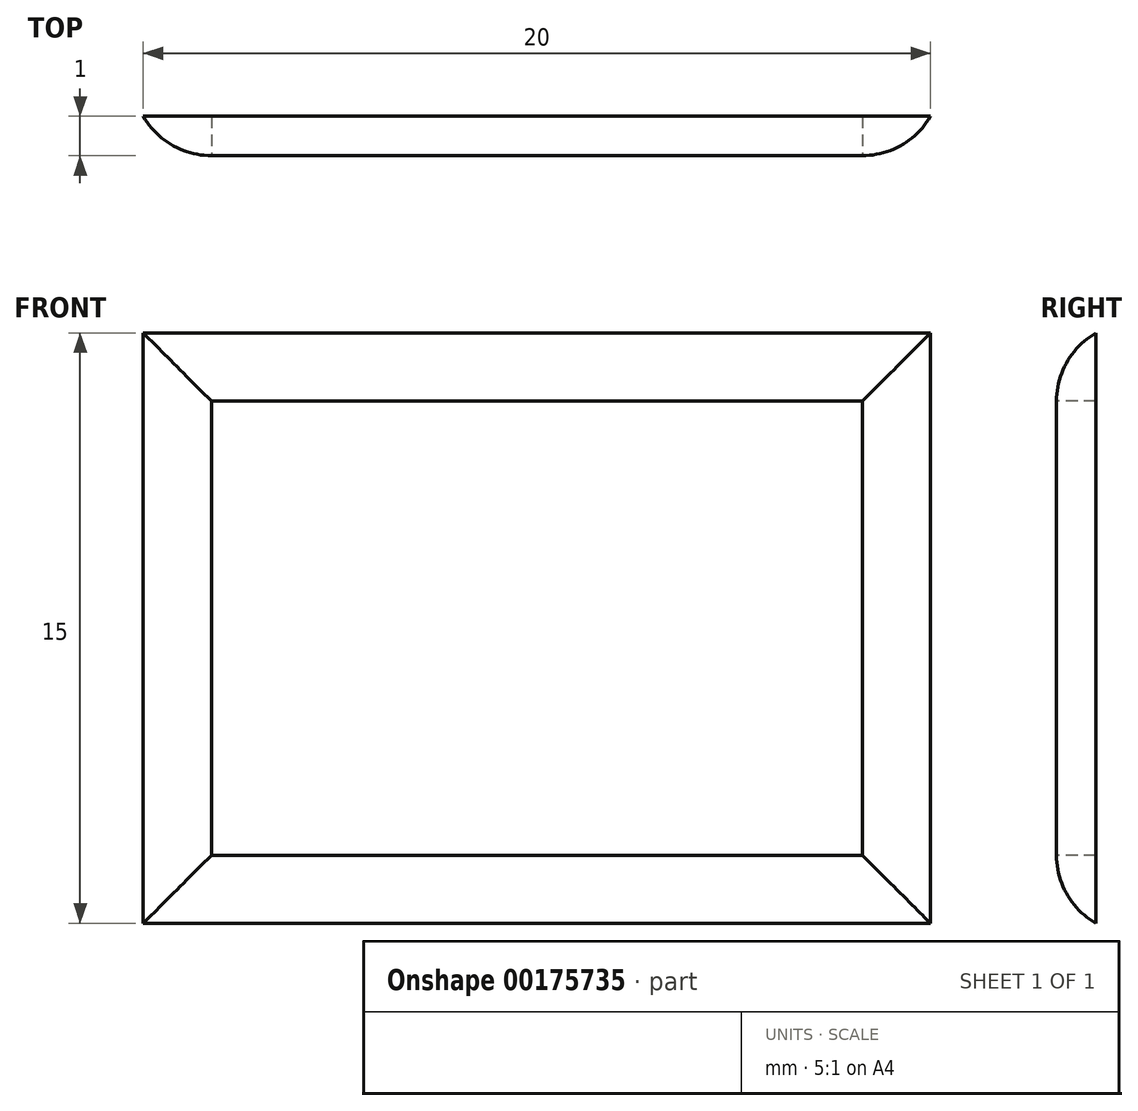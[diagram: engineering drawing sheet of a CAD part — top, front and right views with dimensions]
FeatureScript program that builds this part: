
annotation { "Feature Type Name" : "Feature", "Feature Type Description" : "" }
export const myFeature = defineFeature(function(context is Context, id is Id, definition is map)
    precondition{}
    {
        {
            var Q0;
            Q0=qCreatedBy(makeId("Front.planeOp"),FACE);
            var sketch = newSketch(context, id + "F0", { "sketchPlane" : qUnion([Q0])});
            skLineSegment(sketch, "E0", {"start": v(-7.62, 10.7) * mm, "end": v(12.38, 10.7) * mm});
            skLineSegment(sketch, "E1", {"start": v(12.38, 10.7) * mm, "end": v(12.38, -4.3) * mm});
            skLineSegment(sketch, "E2", {"start": v(12.38, -4.3) * mm, "end": v(-7.62, -4.3) * mm});
            skLineSegment(sketch, "E3", {"start": v(-7.62, -4.3) * mm, "end": v(-7.62, 10.7) * mm});
            skSolve(sketch);
        }
        {
            var Q0;
            Q0=makeQuery(id+"F0.imprint","IMPRINT",FACE,{"disambiguationData":[TD([[makeQuery(id+"F0.imprint","IMPRINT",EDGE,{"derivedFrom":sQuery(id+"F0.wireOp",EDGE,"E0")}),-1.0]])]});
            extrude(context, id + "F1", {"entities" : qUnion([Q0]), "depth" : 1 * mm});
        }
        {
            var Q0;
            Q0=makeQuery(id+"F1.opExtrude","CAP_EDGE",EDGE,{"disambiguationData":[OSD([sQuery(id+"F0.wireOp",EDGE,"E0")])],"isStart":false});
            var Q1;
            Q1=makeQuery(id+"F1.opExtrude","CAP_EDGE",EDGE,{"disambiguationData":[OSD([sQuery(id+"F0.wireOp",EDGE,"E2")])],"isStart":false});
            var Q2;
            Q2=makeQuery(id+"F1.opExtrude","CAP_EDGE",EDGE,{"disambiguationData":[OSD([sQuery(id+"F0.wireOp",EDGE,"E1")])],"isStart":false});
            var Q3;
            Q3=makeQuery(id+"F1.opExtrude","CAP_FACE",FACE,{"disambiguationData":[OSD([sQuery(id+"F0.wireOp",EDGE,"E0"),sQuery(id+"F0.wireOp",EDGE,"E1"),sQuery(id+"F0.wireOp",EDGE,"E2"),sQuery(id+"F0.wireOp",EDGE,"E3")])],"isStart":false});
            fillet(context, id + "F2", {"entities" : qUnion([Q0, Q1, Q2, Q3]), "radius" : 2 * mm, "tangentPropagation" : true, "allowEdgeOverflow" : false});
        }
        {
            var Q0;
            Q0=makeQuery(id+"F1.opExtrude","CAP_FACE",FACE,{"disambiguationData":[OSD([sQuery(id+"F0.wireOp",EDGE,"E0"),sQuery(id+"F0.wireOp",EDGE,"E1"),sQuery(id+"F0.wireOp",EDGE,"E2"),sQuery(id+"F0.wireOp",EDGE,"E3")])],"isStart":false});
            var sketch = newSketch(context, id + "F3", { "sketchPlane" : qUnion([Q0])});
            skLineSegment(sketch, "E4.bottom", {"start": v(-5.89, 8.96) * mm, "end": v(10.65, 8.96) * mm});
            skLineSegment(sketch, "E4.top", {"start": v(-5.89, 8.96) * mm, "end": v(10.65, 8.96) * mm});
            skLineSegment(sketch, "E4.left", {"start": v(-5.89, 8.96) * mm, "end": v(-5.89, 8.96) * mm});
            skLineSegment(sketch, "E4.right", {"start": v(10.65, 8.96) * mm, "end": v(10.65, 8.96) * mm});
            skLineSegment(sketch, "E5.bottom", {"start": v(10.65, -2.57) * mm, "end": v(-5.89, -2.57) * mm});
            skLineSegment(sketch, "E5.top", {"start": v(10.65, 8.96) * mm, "end": v(-5.89, 8.96) * mm});
            skLineSegment(sketch, "E5.left", {"start": v(10.65, -2.57) * mm, "end": v(10.65, 8.96) * mm});
            skLineSegment(sketch, "E5.right", {"start": v(-5.89, -2.57) * mm, "end": v(-5.89, 8.96) * mm});
            skSolve(sketch);
        }
        {
            var Q0;
            Q0 = qSketchRegion(id + "F3", true);
            extrude(context, id + "F4", {"entities" : qUnion([Q0]), "oppositeDirection" : true, "depth" : 1 * mm});
        }
    });
